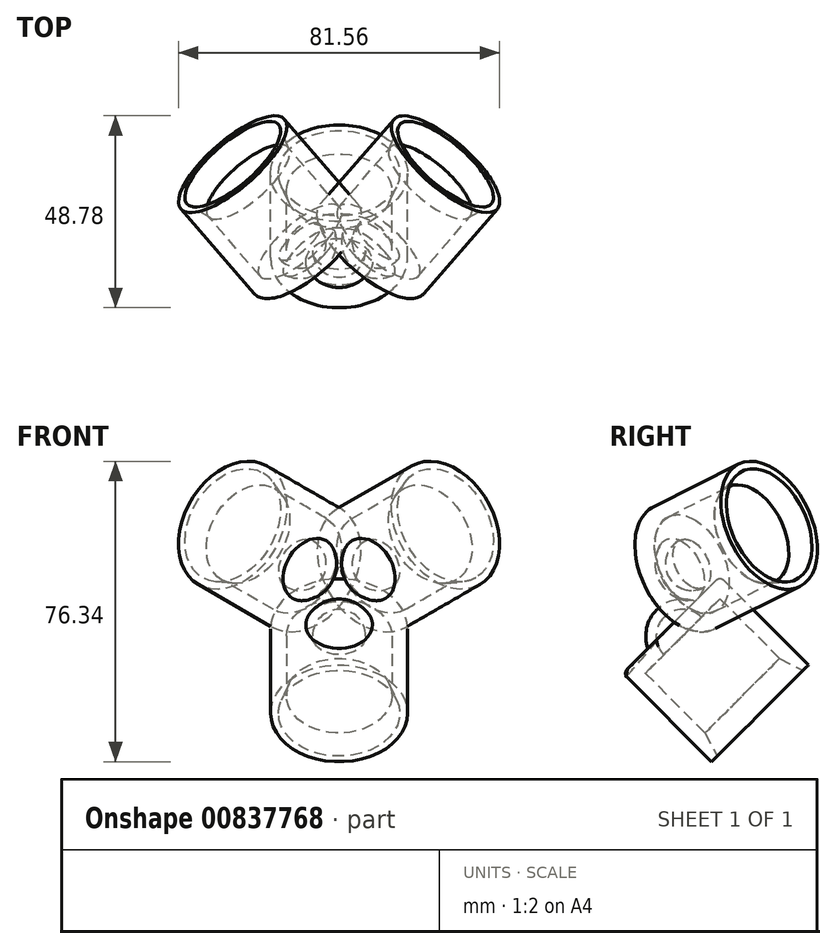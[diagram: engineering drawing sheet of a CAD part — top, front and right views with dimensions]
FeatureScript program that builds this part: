
annotation { "Feature Type Name" : "Feature", "Feature Type Description" : "" }
export const myFeature = defineFeature(function(context is Context, id is Id, definition is map)
    precondition{}
    {
        {
            var Q0;
            Q0=qCreatedBy(makeId("Front.planeOp"),FACE);
            var sketch = newSketch(context, id + "F0", { "sketchPlane" : qUnion([Q0])});
            skLineSegment(sketch, "E0", {"start": v(-65.6, 0) * mm, "end": v(95.42, 0) * mm, "construction": true});
            skLineSegment(sketch, "E1.left", {"start": v(-13.4, 12.88) * mm, "end": v(-13.4, -12.88) * mm, "construction": true});
            skLineSegment(sketch, "E1.right", {"start": v(13.39, 12.88) * mm, "end": v(13.4, -8.56) * mm});
            skPoint(sketch, "E1.middle", {"position": v(0, 0) * mm});
            skLineSegment(sketch, "E2.left", {"start": v(-15.41, 14.9) * mm, "end": v(-15.41, -14.9) * mm, "construction": true});
            skLineSegment(sketch, "E3", {"start": v(15.41, 14.9) * mm, "end": v(0, 41.6) * mm, "construction": true});
            skLineSegment(sketch, "E4", {"start": v(-15.41, 14.9) * mm, "end": v(0, 41.6) * mm, "construction": true});
            skPoint(sketch, "E5", {"position": v(0, 23.8) * mm});
            skPoint(sketch, "E6.endSnap0", {"position": v(7.7, 14.9) * mm});
            skPoint(sketch, "E7", {"position": v(0, 12.88) * mm});
            skPoint(sketch, "E8", {"position": v(0, 14.9) * mm});
            skLineSegment(sketch, "E9", {"start": v(9.37, 12.88) * mm, "end": v(13.39, 12.88) * mm});
            skLineSegment(sketch, "E10", {"start": v(-13.4, 12.88) * mm, "end": v(9.37, 12.88) * mm, "construction": true});
            skLineSegment(sketch, "E11", {"start": v(-15.41, 14.9) * mm, "end": v(9.37, 14.9) * mm, "construction": true});
            skLineSegment(sketch, "E12", {"start": v(0, 0) * mm, "end": v(0, 25.56) * mm, "construction": true});
            skArc(sketch, "E13", {"start": v(6.73, 12.88) * mm, "mid": v(4.76, 17.64) * mm, "end": v(0, 19.61) * mm});
            skArc(sketch, "E14", {"start": v(8.47, 16.88) * mm, "mid": v(5.01, 20.8) * mm, "end": v(0, 22.25) * mm});
            skLineSegment(sketch, "E15", {"start": v(9.37, 12.88) * mm, "end": v(6.73, 12.88) * mm});
            skLineSegment(sketch, "E16", {"start": v(0, 22.25) * mm, "end": v(0, 19.61) * mm});
            skLineSegment(sketch, "E17", {"start": v(13.39, 7.3) * mm, "end": v(17.4, 7.3) * mm, "construction": true});
            skLineSegment(sketch, "E18", {"start": v(17.4, 16.88) * mm, "end": v(17.4, -14.9) * mm});
            skLineSegment(sketch, "E19", {"start": v(15.4, -14.9) * mm, "end": v(17.4, -14.9) * mm});
            skLineSegment(sketch, "E20", {"start": v(17.4, 16.88) * mm, "end": v(8.47, 16.88) * mm});
            skPoint(sketch, "E21.orphan", {"position": v(17.4, 14.9) * mm});
            skLineSegment(sketch, "E22", {"start": v(15.4, -14.9) * mm, "end": v(13.39, -8.56) * mm});
            skPoint(sketch, "E23.end.orphan", {"position": v(13.4, -14.9) * mm});
            skSolve(sketch);
        }
        {
            var Q0;
            Q0=makeQuery(id+"F0.imprint","IMPRINT",FACE,{"disambiguationData":[TD([[makeQuery(id+"F0.imprint","IMPRINT",EDGE,{"derivedFrom":sQuery(id+"F0.wireOp",EDGE,"E1.right")}),1.0]])]});
            var Q1;
            Q1=sQuery(id+"F0.wireOp",EDGE,"E12");
            revolve(context, id + "F1", {"surfaceOperationType" : NewSurfaceOperationType.NEW, "entities" : qUnion([Q0]), "axis" : qUnion([Q1]), "revolveType" : RevolveType.FULL});
        }
        {
            var Q0;
            Q0=makeQuery(id+"F1.opRevolve","SWEPT_EDGE",EDGE,{"disambiguationData":[OSD([sQuery(id+"F0.wireOp",EDGE,"E18"),sQuery(id+"F0.wireOp",EDGE,"E20")])]});
            fillet(context, id + "F2", {"entities" : qUnion([Q0]), "radius" : 1.5 * mm, "tangentPropagation" : true, "allowEdgeOverflow" : false});
        }
        {
            var Q0;
            Q0=qCreatedBy(makeId("Right.planeOp"),FACE);
            var sketch = newSketch(context, id + "F3", { "sketchPlane" : qUnion([Q0])});
            skLineSegment(sketch, "E24", {"start": v(-35.53, 26) * mm, "end": v(8.3, 26) * mm, "construction": true});
            skLineSegment(sketch, "E25", {"start": v(8.28, 30.68) * mm, "end": v(-35.5, 30.68) * mm, "construction": true});
            skSolve(sketch);
        }
        {
            var Q0;
            Q0=makeQuery(id+"F1.opRevolve","SWEPT_BODY",BODY,{"disambiguationData":[OSD([sQuery(id+"F0.wireOp",EDGE,"E1.right"),sQuery(id+"F0.wireOp",EDGE,"E2.right"),sQuery(id+"F0.wireOp",EDGE,"E23"),sQuery(id+"F0.wireOp",EDGE,"bP7MgH2K-PIgu-sQjO-5KmN-4AKa93nuKyW7"),sQuery(id+"F0.wireOp",EDGE,"E6"),sQuery(id+"F0.wireOp",EDGE,"L42gxlVk-bAQj-lGxW-YQ5i-IcCWysg2b6hQ"),sQuery(id+"F0.wireOp",EDGE,"E9")])]});
            var Q1;
            Q1=sQuery(id+"F3.wireOp",EDGE,"E24");
            circularPattern(context, id + "F4", {"entities" : qUnion([Q0]), "axis" : qUnion([Q1]), "angle" : 360 * degree, "instanceCount" : 3, "equalSpace" : true});
        }
        {
            var Q0;
            Q0=makeQuery(id+"F1.opRevolve","SWEPT_BODY",BODY,{"disambiguationData":[OSD([sQuery(id+"F0.wireOp",EDGE,"E1.right"),sQuery(id+"F0.wireOp",EDGE,"E2.right"),sQuery(id+"F0.wireOp",EDGE,"u6sGE5v3-QqYS-glfV-MdEO-LVSjNsrG9YqO"),sQuery(id+"F0.wireOp",EDGE,"e8LDt0c8-95OP-7SPG-cx0F-moiXSnHBQ2JR"),sQuery(id+"F0.wireOp",EDGE,"Aw2z7rFZ-ruUb-1NY8-J7V9-fNkVEHLTtg4K"),sQuery(id+"F0.wireOp",EDGE,"E23"),sQuery(id+"F0.wireOp",EDGE,"bP7MgH2K-PIgu-sQjO-5KmN-4AKa93nuKyW7")])]});
            var Q1;
            Q1=sQuery(id+"F0.wireOp",EDGE,"E11");
            transform(context, id + "F5", {"entities" : qUnion([Q0]), "transformType" : TransformType.ROTATION, "transformAxis" : qUnion([Q1]), "angle" : 45 * degree, "makeCopy" : false});
        }
        {
            var Q0;
            Q0=makeQuery(id+"F4.opPattern","COPY",BODY,{"derivedFrom":makeQuery(id+"F1.opRevolve","SWEPT_BODY",BODY,{"disambiguationData":[OSD([sQuery(id+"F0.wireOp",EDGE,"E1.right"),sQuery(id+"F0.wireOp",EDGE,"E2.right"),sQuery(id+"F0.wireOp",EDGE,"u6sGE5v3-QqYS-glfV-MdEO-LVSjNsrG9YqO"),sQuery(id+"F0.wireOp",EDGE,"e8LDt0c8-95OP-7SPG-cx0F-moiXSnHBQ2JR"),sQuery(id+"F0.wireOp",EDGE,"Aw2z7rFZ-ruUb-1NY8-J7V9-fNkVEHLTtg4K"),sQuery(id+"F0.wireOp",EDGE,"E23"),sQuery(id+"F0.wireOp",EDGE,"bP7MgH2K-PIgu-sQjO-5KmN-4AKa93nuKyW7")])]}),"instanceName":"1"});
            var Q1;
            Q1=sQuery(id+"F0.wireOp",EDGE,"E4");
            transform(context, id + "F6", {"entities" : qUnion([Q0]), "transformType" : TransformType.ROTATION, "transformAxis" : qUnion([Q1]), "angle" : 45 * degree, "oppositeDirection" : true, "makeCopy" : false});
        }
        {
            var Q0;
            Q0=makeQuery(id+"F4.opPattern","COPY",BODY,{"derivedFrom":makeQuery(id+"F1.opRevolve","SWEPT_BODY",BODY,{"disambiguationData":[OSD([sQuery(id+"F0.wireOp",EDGE,"E1.right"),sQuery(id+"F0.wireOp",EDGE,"E2.right"),sQuery(id+"F0.wireOp",EDGE,"u6sGE5v3-QqYS-glfV-MdEO-LVSjNsrG9YqO"),sQuery(id+"F0.wireOp",EDGE,"e8LDt0c8-95OP-7SPG-cx0F-moiXSnHBQ2JR"),sQuery(id+"F0.wireOp",EDGE,"Aw2z7rFZ-ruUb-1NY8-J7V9-fNkVEHLTtg4K"),sQuery(id+"F0.wireOp",EDGE,"E23"),sQuery(id+"F0.wireOp",EDGE,"bP7MgH2K-PIgu-sQjO-5KmN-4AKa93nuKyW7")])]}),"instanceName":"2"});
            var Q1;
            Q1=sQuery(id+"F0.wireOp",EDGE,"E3");
            transform(context, id + "F7", {"entities" : qUnion([Q0]), "transformType" : TransformType.ROTATION, "transformAxis" : qUnion([Q1]), "angle" : 45 * degree, "makeCopy" : false});
        }
        {
            var Q0;
            Q0=makeQuery(id+"F1.opRevolve","SWEPT_BODY",BODY,{"disambiguationData":[OSD([sQuery(id+"F0.wireOp",EDGE,"E1.right"),sQuery(id+"F0.wireOp",EDGE,"E2.right"),sQuery(id+"F0.wireOp",EDGE,"E23"),sQuery(id+"F0.wireOp",EDGE,"bP7MgH2K-PIgu-sQjO-5KmN-4AKa93nuKyW7"),sQuery(id+"F0.wireOp",EDGE,"L42gxlVk-bAQj-lGxW-YQ5i-IcCWysg2b6hQ"),sQuery(id+"F0.wireOp",EDGE,"E9"),sQuery(id+"F0.wireOp",EDGE,"E13"),sQuery(id+"F0.wireOp",EDGE,"E14"),sQuery(id+"F0.wireOp",EDGE,"E15"),sQuery(id+"F0.wireOp",EDGE,"E16")])]});
            transform(context, id + "F8", {"entities" : qUnion([Q0]), "transformType" : TransformType.COPY});
        }
        {
            var Q0;
            Q0=makeQuery(id+"F8.opPattern","COPY",BODY,{"derivedFrom":makeQuery(id+"F1.opRevolve","SWEPT_BODY",BODY,{"disambiguationData":[OSD([sQuery(id+"F0.wireOp",EDGE,"E1.right"),sQuery(id+"F0.wireOp",EDGE,"E2.right"),sQuery(id+"F0.wireOp",EDGE,"E23"),sQuery(id+"F0.wireOp",EDGE,"bP7MgH2K-PIgu-sQjO-5KmN-4AKa93nuKyW7"),sQuery(id+"F0.wireOp",EDGE,"L42gxlVk-bAQj-lGxW-YQ5i-IcCWysg2b6hQ"),sQuery(id+"F0.wireOp",EDGE,"E9"),sQuery(id+"F0.wireOp",EDGE,"E13"),sQuery(id+"F0.wireOp",EDGE,"E14"),sQuery(id+"F0.wireOp",EDGE,"E15"),sQuery(id+"F0.wireOp",EDGE,"E16")])]}),"instanceName":"1"});
            deleteBodies(context, id + "F9", {"entities" : qUnion([Q0])});
        }
    });
